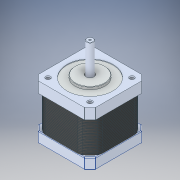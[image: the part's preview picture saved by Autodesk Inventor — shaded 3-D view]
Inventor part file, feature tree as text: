
AUTODESK INVENTOR PART (.ipt)
format: ipt  version: 2019 (Build 230136000, 136)  size: 1,032,704 bytes
history: mixed  units: in
note: dims shown in document units (in); Inventor stores cm internally (conversion verified against a paired STEP export)
features: chamfer x26, fillet x1, imported_body x1
ambient origin geometry x8: Origin, YZ Plane, XZ Plane, XY Plane, X Axis, Y Axis, Z Axis, Center Point
bodies: Solid1 (imported_parasolid), Solid2 (imported_parasolid), Solid3 (imported_parasolid), Solid4 (imported_parasolid), Solid5 (imported_parasolid), Solid6 (imported_parasolid), Solid7 (imported_parasolid), Solid8 (imported_parasolid), Solid9 (imported_parasolid), Solid10 (imported_parasolid), Solid11 (imported_parasolid), Solid12 (imported_parasolid), Solid13 (imported_parasolid), Solid14 (imported_parasolid), Solid15 (imported_parasolid), Solid16 (imported_parasolid), Solid17 (imported_parasolid), Solid18 (imported_parasolid), Solid19 (imported_parasolid), Solid20 (imported_parasolid), Solid21 (imported_parasolid), Solid22 (imported_parasolid), Solid23 (imported_parasolid), Solid24 (imported_parasolid), Solid25 (imported_parasolid), Solid26 (imported_parasolid), Solid27 (imported_parasolid)
feature tree (28):
  fillet  "Redondeo1"  [1 undecoded]
  chamfer  "Chaflán1"  [1 undecoded]
  chamfer  "Chaflán5"  [1 undecoded]
  chamfer  "Chaflán6"  [1 undecoded]
  chamfer  "Chaflán7"  [1 undecoded]
  chamfer  "Chaflán8"  [1 undecoded]
  chamfer  "Chaflán9"  [1 undecoded]
  chamfer  "Chaflán10"  [1 undecoded]
  chamfer  "Chaflán11"  [1 undecoded]
  chamfer  "Chaflán12"  [1 undecoded]
  chamfer  "Chaflán13"  [1 undecoded]
  chamfer  "Chaflán14"  [1 undecoded]
  chamfer  "Chaflán15"  [1 undecoded]
  chamfer  "Chaflán16"  [1 undecoded]
  chamfer  "Chaflán17"  [1 undecoded]
  chamfer  "Chaflán18"  [1 undecoded]
  chamfer  "Chaflán19"  [1 undecoded]
  chamfer  "Chaflán20"  [1 undecoded]
  chamfer  "Chaflán21"  [1 undecoded]
  chamfer  "Chaflán22"  [1 undecoded]
  chamfer  "Chaflán23"  [1 undecoded]
  chamfer  "Chaflán24"  [1 undecoded]
  chamfer  "Chaflán25"  [1 undecoded]
  chamfer  "Chaflán26"  [1 undecoded]
  chamfer  "Chaflán27"  [1 undecoded]
  chamfer  "Chaflán28"  [1 undecoded]
  chamfer  "Chaflán29"  [1 undecoded]
  imported_body  NMx_Import_Brep_tag  [imported B-rep: ~1302 faces, bbox_mm=[42.3, 64.2, 42.3]]
note: 27 required parameter values undecoded (feature->parameter linkage not recoverable at this tier; creation-order binding heuristic only, values carry confidence <= 0.55)
